# Revit family: Qmax 550(Shrd)
name_source: partatom
category: Plumbing Fixtures
revit_build: Autodesk Revit 2013 (Build: 20120221_2030(x64)
units: mm (PartAtom-declared; Revit-internal decimal feet)

## types (5) — shared parameters
ACO Hydraulic Design Software = http://www.acodesign.co.uk
Assembly Code = D2040
Chamber Connector - Channel Colour = Black
Chamber Connector - Channel Material = Medium Density Polyethylene
Chamber Connector - Dimensions = Female End=800mm x 665mm x 740mm, Male End=800mm x 665mm x 690mm  (LxWXH)
Chamber Connector - Model Description = High capacity slot drainage channel system
Chamber Connector - Product Code = 32826
Chamber Connector - Recyclable = Fully recyclable
Chamber Connector - Recycled Material Content = Variable %
Chamber Connector - Weight = 11.8 kg
Channel Colour = Black
Channel Material = Medium Density Polyethylene
Channel Recyclable = Fully recyclable
Channel Recycled Material Content = Variable %
Closing End Cap - Colour = Black
Closing End Cap - Dimensions = 635mm x 12mm x 715mm (LxWxH)
Closing End Cap - Material = High Density Polyethylene
Closing End Cap - Model Description = High capacity slot drainage channel system
Closing End Cap - Product Code = 32825
Closing End Cap - Recyclable = Fully recyclable
Closing End Cap - Recycled Material Content = 0%
Closing End Cap - Weight = 3.5 kg
Concrete Surround Volume - Load Class A 15 - D 400 = 0.455 m³/m
Concrete Surround Volume - Load Class E 600 - F 900 = 0.60 m³/m
Edge Rail Recyclable = Fully recyclable
Edge Rail Recycled Material Content = Between 40% - 90%
Hydraulic Performance = http://www.aco.co.uk
Installation - Concrete Grade = Refer to brochure
Installation - Reinforcement Details = Refer to brochure
Installation Guidelines = http://www.aco.co.uk
Length = 2000 mm  [stored 6.56168 ft]
Load Class = A 15 - F 900
Maintenance Guidelines = http://www.aco.co.uk
Manufacturer = ACO Technologies plc - ACO Water Management Division
Model = ACO Qmax 550
Model Description = High capacity slot drainage channel system
Price = POA - contact ACO
Product Brochure = http://www.aco.co.uk
Product Page URL = http://www.aco.co.uk
Product Standard = BS EN 1433:2002 CE  marked
Revision = 1
Seal Colour = Black
Seal Material = EPDM
Seal Recyclable = Fully recyclable
Seal Recycled Material Content = 0%
Telephone = +44 (0)1462 816666
URL = www.aco.co.uk
Width Overall = 635 mm
zero-valued in all types: Cost, SerialNumber, TagNumber

## per-type parameters (varying)
| type | ChamberOrigin | Channel C.S.A | Depth Overall | Drainage Slot Intake Area | Drainage Slot Width | E1-QFlow-DuctileIron | E2-QGuard-DuctileIron | E3-QFlow-GalvSteel | E4-QGuard-GalvSteel | E5-QSlot-GalvSteel | Edge Rail Colour | Edge Rail Finish | Edge Rail Material | End Cap Distance | Fax | Floor Opening Width | Invert Depth | Material | Product Code | Product Dimensions | Product Weight | Type Comments | V_CoarseE1 | V_Coarse_E5 |
| 32820 - Q-Flow Edge - D.I | 443 mm | 154202mm² | 920 mm  [stored 3.01837 ft] | 18775mm²/m | 26mm | Yes | No | No | No | No | Black | ATec coating | Ductile Iron | 533 mm | +44 (0)1462 815895 | 65 mm  [stored 0.213255 ft] | 800mm | Iron, Ductile | 32820 | 2000mm x 635mm x 920mm (LxWxH) | 44 kg | ACO Qmax 550 channel assembly complete with ACO Q-Flow ductile iron edge rail | Yes | No |
| 32821 - Q-Guard Edge - D.I | 443 mm | 154202mm²
154202mm² | 920 mm  [stored 3.01837 ft] | 10925mm²/m | 8mm twin slot | No | Yes | No | No | No | Black | ATec coating | Ductile Iron | 533 mm | +44 (0)1462 815895 | 65 mm  [stored 0.213255 ft] | 800mm | Iron, Ductile | 32821 | 2000mm x 635mm x 920mm (LxWxH) | 45 kg | ACO Qmax 550 channel assembly complete with ACO Q-Guard ductile iron edge rail | Yes | No |
| 32822 - Q-Flow Edge - G.S | 443 mm | 154202mm² | 920 mm  [stored 3.01837 ft] | 18106mm²/m | 26mm | No | No | Yes | No | No | Silver
Silver | Galvanised | Steel | 533 mm | +44 (0)1462 815895 | 90 mm  [stored 0.295276 ft] | 800mm | Steel, Galvanized | 32822 | 2000mm x 635mm x 920mm (LxWxH) | 35.6 kg | ACO Qmax 550 channel assembly complete with ACO Q-Flow galvanised steel edge rail | Yes | No |
| 32823 - Q-Guard Edge - G.S | 443 mm | 154202mm² | 920 mm  [stored 3.01837 ft] | 8356mm²/m | 10mm | No | No | No | Yes | No | Silver | Galvanised | Steel | 533 mm | +44 (0)1462 815895 | 55 mm  [stored 0.180446 ft] | 800mm | Steel, Galvanized | 32823 | 2000mm x 635mm x 920mm (LxWxH) | 33.1 kg | ACO Qmax 550 channel assembly complete with ACO Q-Guard galvanised steel edge rail | Yes | No |
| 32824 - Q-Slot Edge - G.S | 543 mm | 154202mm² | 1020 mm  [stored 3.34646 ft] | 10000mm²/m | 10mm | No | No | No | No | Yes | Silver | Galvanised | Steel | 633 mm | +44 (0)1462 815895
+44 (0)1462 815895 | 18 mm  [stored 0.0590551 ft] | 900mm | Steel, Galvanized | 32824 | 2000mm x 635mm x 1020mm (LxWxH) | 40.7 kg | ACO Qmax 550 channel assembly complete with ACO Q-Slot galvanised steel edge rail | No | Yes |

note: [stored X ft] marks values corroborated as IEEE doubles in the binary element streams (Revit-internal decimal feet)

## geometry (parser evidence)
native form markers: Blend x4, Sweep x13
no freeform markers — native parametric forms only
